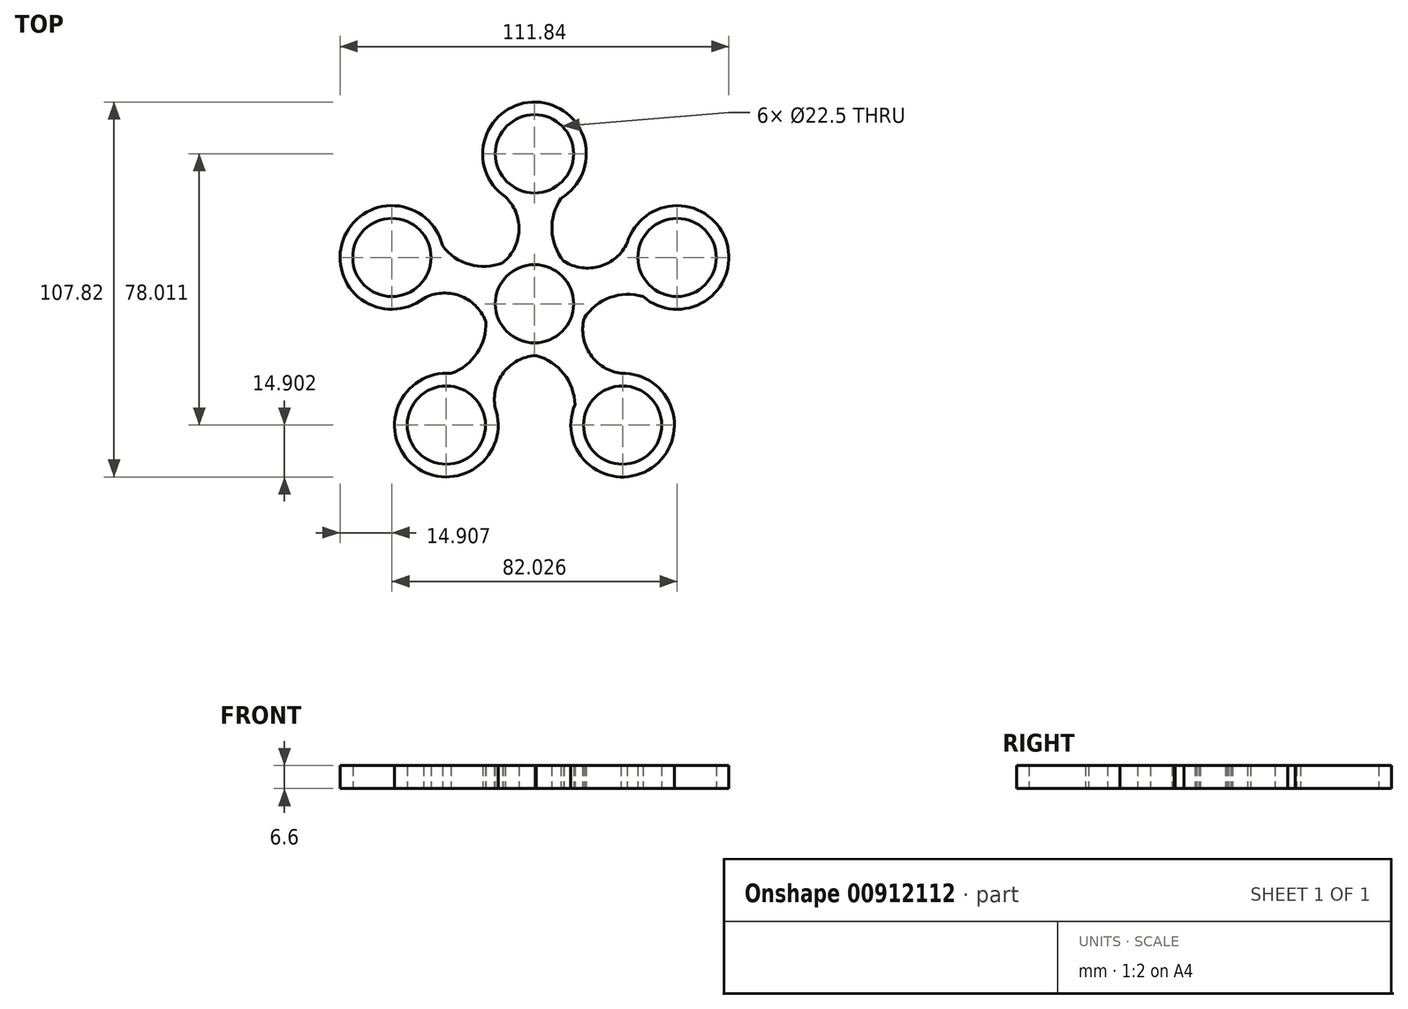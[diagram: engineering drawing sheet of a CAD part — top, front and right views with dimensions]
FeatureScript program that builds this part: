
annotation { "Feature Type Name" : "Feature", "Feature Type Description" : "" }
export const myFeature = defineFeature(function(context is Context, id is Id, definition is map)
    precondition{}
    {
        {
            var Q0;
            Q0=qCreatedBy(makeId("Top.planeOp"),FACE);
            var sketch = newSketch(context, id + "F0", { "sketchPlane" : qUnion([Q0])});
            skCircle(sketch, "E0", {"center": v(0, 0) * mm, "radius": 11.25 * mm});
            skCircle(sketch, "E1", {"center": v(0, 43.12) * mm, "radius": 11.25 * mm});
            skArc(sketch, "E2", {"start": v(-8.97, 11.9) * mm, "mid": v(0.36, -14.9) * mm, "end": v(8.39, 12.32) * mm});
            skArc(sketch, "E3", {"start": v(7.66, 30.34) * mm, "mid": v(0.44, 58.02) * mm, "end": v(-8.41, 30.82) * mm});
            skArc(sketch, "E4", {"start": v(-8.97, 11.9) * mm, "mid": v(-4.44, 21.24) * mm, "end": v(-8.41, 30.82) * mm});
            skArc(sketch, "E5", {"start": v(7.66, 30.34) * mm, "mid": v(5.01, 21.2) * mm, "end": v(8.39, 12.32) * mm});
            skArc(sketch, "E6.1.0", {"start": v(-14.1, -4.85) * mm, "mid": v(-21.57, 2.34) * mm, "end": v(-31.91, 1.52) * mm});
            skArc(sketch, "E6.1.1", {"start": v(-26.49, 16.67) * mm, "mid": v(-18.62, 11.32) * mm, "end": v(-9.12, 11.78) * mm});
            skArc(sketch, "E6.1.2", {"start": v(-26.49, 16.67) * mm, "mid": v(-55.04, 18.35) * mm, "end": v(-31.91, 1.52) * mm});
            skCircle(sketch, "E6.1.3", {"center": v(-41.01, 13.33) * mm, "radius": 11.25 * mm});
            skArc(sketch, "E6.2.0", {"start": v(0.26, -14.9) * mm, "mid": v(-8.9, -19.8) * mm, "end": v(-11.31, -29.88) * mm});
            skArc(sketch, "E6.2.1", {"start": v(-24.04, -20.04) * mm, "mid": v(-16.52, -14.21) * mm, "end": v(-14.03, -5.04) * mm});
            skArc(sketch, "E6.2.2", {"start": v(-24.04, -20.04) * mm, "mid": v(-34.46, -46.68) * mm, "end": v(-11.31, -29.88) * mm});
            skCircle(sketch, "E6.2.3", {"center": v(-25.35, -34.89) * mm, "radius": 11.25 * mm});
            skArc(sketch, "E6.3.0", {"start": v(14.25, -4.36) * mm, "mid": v(16.07, -14.57) * mm, "end": v(24.92, -20) * mm});
            skArc(sketch, "E6.3.1", {"start": v(11.63, -29.05) * mm, "mid": v(8.41, -20.1) * mm, "end": v(0.46, -14.9) * mm});
            skArc(sketch, "E6.3.2", {"start": v(11.63, -29.05) * mm, "mid": v(33.74, -47.2) * mm, "end": v(24.92, -20) * mm});
            skCircle(sketch, "E6.3.3", {"center": v(25.35, -34.89) * mm, "radius": 11.25 * mm});
            skArc(sketch, "E6.4.0", {"start": v(8.55, 12.2) * mm, "mid": v(18.83, 10.78) * mm, "end": v(26.71, 17.53) * mm});
            skArc(sketch, "E6.4.1", {"start": v(31.23, 2.09) * mm, "mid": v(21.72, 1.79) * mm, "end": v(14.3, -4.17) * mm});
            skArc(sketch, "E6.4.2", {"start": v(31.23, 2.09) * mm, "mid": v(55.32, 17.5) * mm, "end": v(26.71, 17.53) * mm});
            skCircle(sketch, "E6.4.3", {"center": v(41.01, 13.33) * mm, "radius": 11.25 * mm});
            skSolve(sketch);
        }
        {
            var Q0;
            {var subQ1=sQuery(id+"F0.wireOp",EDGE,"E6.1.0");Q0=makeQuery(id+"F0.imprint","IMPRINT",FACE,{"disambiguationData":[TD([[makeQuery(id+"F0.imprint","IMPRINT",EDGE,{"derivedFrom":subQ1}),-1.0]])]});}
            var Q1;
            {var subQ1=sQuery(id+"F0.wireOp",EDGE,"E6.2.0");Q1=makeQuery(id+"F0.imprint","IMPRINT",FACE,{"disambiguationData":[TD([[makeQuery(id+"F0.imprint","IMPRINT",EDGE,{"derivedFrom":subQ1}),-1.0]])]});}
            var Q2;
            {var subQ1=sQuery(id+"F0.wireOp",EDGE,"E6.3.0");Q2=makeQuery(id+"F0.imprint","IMPRINT",FACE,{"disambiguationData":[TD([[makeQuery(id+"F0.imprint","IMPRINT",EDGE,{"derivedFrom":subQ1}),-1.0]])]});}
            var Q3;
            {var subQ1=sQuery(id+"F0.wireOp",EDGE,"E6.4.0");Q3=makeQuery(id+"F0.imprint","IMPRINT",FACE,{"disambiguationData":[TD([[makeQuery(id+"F0.imprint","IMPRINT",EDGE,{"derivedFrom":subQ1}),-1.0]])]});}
            var Q4;
            Q4=makeQuery(id+"F0.imprint","IMPRINT",FACE,{"disambiguationData":[TD([[makeQuery(id+"F0.imprint","IMPRINT",EDGE,{"derivedFrom":sQuery(id+"F0.wireOp",EDGE,"E0")}),-1.0]])]});
            extrude(context, id + "F1", {"entities" : qUnion([Q0, Q1, Q2, Q3, Q4]), "depth" : 6.6 * mm, "offsetDistance" : 25.4 * mm});
        }
    });
